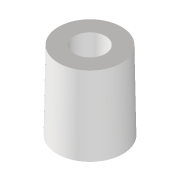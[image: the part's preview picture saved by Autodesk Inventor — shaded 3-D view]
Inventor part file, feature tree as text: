
AUTODESK INVENTOR PART (.ipt)
format: ipt  version: 2022 (Build 260153000, 153)  size: 93,184 bytes
history: native  units: mm
features: extrude x1, sketch x1
ambient origin geometry x8: Origin, YZ Plane, XZ Plane, XY Plane, X Axis, Y Axis, Z Axis, Center Point
bodies: Volumenkörper1 (feature_tree)
feature tree (2):
  extrude  "Extrusion1"  Depth=5.0mm
  sketch  "Skizze1"  dims[d0=1.8mm d1=4.2mm d2=5.0mm d3=-0.174533mm]
